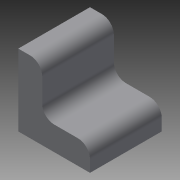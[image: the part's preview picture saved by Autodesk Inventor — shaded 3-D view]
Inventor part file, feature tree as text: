
AUTODESK INVENTOR PART (.ipt)
format: ipt  version: 2015 (Build 190159000, 159)  size: 89,088 bytes
history: native  units: in
note: dims shown in document units (in); Inventor stores cm internally (conversion verified against a paired STEP export)
features: fillet x3, extrude x1, sketch x1
ambient origin geometry x8: Origin, YZ Plane, XZ Plane, XY Plane, X Axis, Y Axis, Z Axis, Center Point
bodies: Solid1 (feature_tree)
feature tree (5):
  extrude  "Extrusion1"  Depth=1.0in
  fillet  "Fillet1"  Radius=1.5in
  fillet  "Fillet2"  Radius=0.5in
  fillet  "Fillet3"  Radius=1.5in
  sketch  "Sketch1"  dims[d0=1.5in d1=1.0in d2=1.5in d3=0.5in d4=1.5in d5=0.0in d6=0.25in d7=0.25in d8=0.25in]
